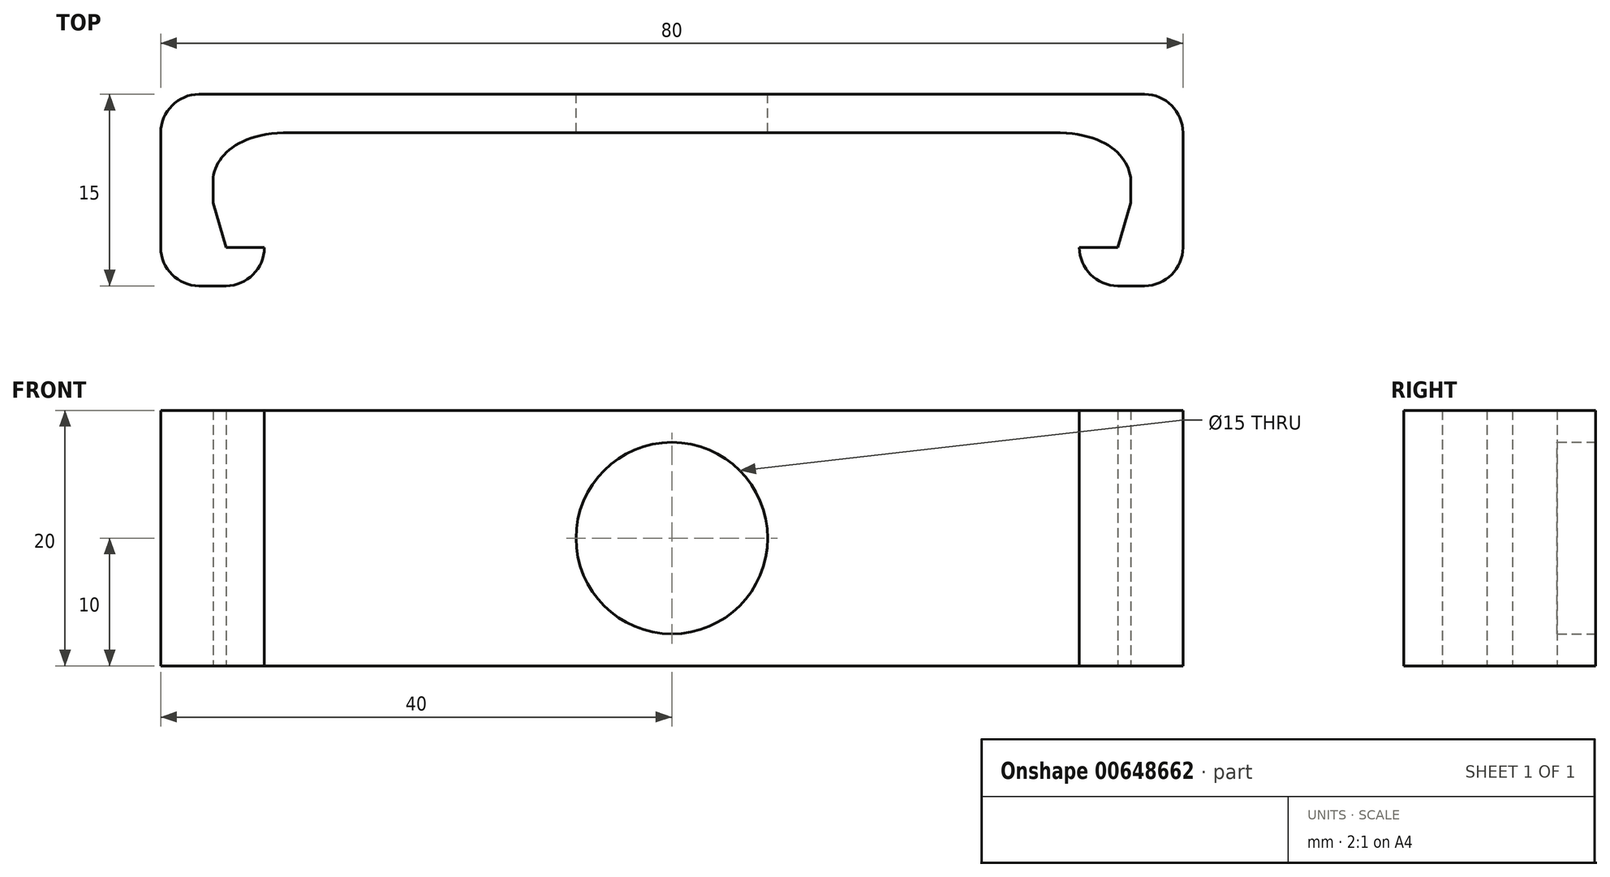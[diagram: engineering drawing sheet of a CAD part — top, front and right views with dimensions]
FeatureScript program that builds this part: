
annotation { "Feature Type Name" : "Feature", "Feature Type Description" : "" }
export const myFeature = defineFeature(function(context is Context, id is Id, definition is map)
    precondition{}
    {
        {
            var Q0;
            Q0=qCreatedBy(makeId("Top.planeOp"),FACE);
            var sketch = newSketch(context, id + "F0", { "sketchPlane" : qUnion([Q0])});
            skLineSegment(sketch, "E0.bottom", {"start": v(37, 7.5) * mm, "end": v(-37, 7.5) * mm});
            skLineSegment(sketch, "E0.top", {"start": v(37, -7.5) * mm, "end": v(34.9, -7.5) * mm});
            skLineSegment(sketch, "E0.left", {"start": v(40, 4.5) * mm, "end": v(40, -4.5) * mm});
            skLineSegment(sketch, "E0.right", {"start": v(-40, 4.5) * mm, "end": v(-40, -4.5) * mm});
            skPoint(sketch, "E0.middle", {"position": v(0, 0) * mm});
            skLineSegment(sketch, "E1.bottom", {"start": v(29.9, 4.5) * mm, "end": v(-29.9, 4.5) * mm});
            skLineSegment(sketch, "E1.top", {"start": v(34.9, -4.5) * mm, "end": v(31.9, -4.5) * mm});
            skLineSegment(sketch, "E1.left", {"start": v(35.9, 1) * mm, "end": v(35.9, -1) * mm});
            skLineSegment(sketch, "E1.right", {"start": v(-35.9, 1) * mm, "end": v(-35.9, -1) * mm});
            skLineSegment(sketch, "E2", {"start": v(-31.9, -4.5) * mm, "end": v(-31.9, -4.5) * mm});
            skLineSegment(sketch, "E3.MirrorCS", {"start": v(31.9, -4.5) * mm, "end": v(31.9, -4.5) * mm});
            skLineSegment(sketch, "E4.trimOffspring", {"start": v(-34.9, -7.5) * mm, "end": v(-37, -7.5) * mm});
            skLineSegment(sketch, "E5.trimOffspring", {"start": v(-31.9, -4.5) * mm, "end": v(-34.9, -4.5) * mm});
            skPoint(sketch, "E6.visualSharp", {"position": v(-40, 7.5) * mm});
            skArc(sketch, "E6.filletArc", {"start": v(-37, 7.5) * mm, "mid": v(-39.12, 6.62) * mm, "end": v(-40, 4.5) * mm});
            skPoint(sketch, "E7.visualSharp", {"position": v(40, 7.5) * mm});
            skArc(sketch, "E7.filletArc", {"start": v(40, 4.5) * mm, "mid": v(39.12, 6.62) * mm, "end": v(37, 7.5) * mm});
            skPoint(sketch, "E8.visualSharp", {"position": v(40, -7.5) * mm});
            skArc(sketch, "E8.filletArc", {"start": v(37, -7.5) * mm, "mid": v(39.12, -6.62) * mm, "end": v(40, -4.5) * mm});
            skPoint(sketch, "E9.visualSharp", {"position": v(-31.9, -7.5) * mm});
            skArc(sketch, "E9.filletArc", {"start": v(-34.9, -7.5) * mm, "mid": v(-32.78, -6.62) * mm, "end": v(-31.9, -4.5) * mm});
            skPoint(sketch, "E10.visualSharp", {"position": v(31.9, -7.5) * mm});
            skArc(sketch, "E10.filletArc", {"start": v(31.9, -4.5) * mm, "mid": v(32.78, -6.62) * mm, "end": v(34.9, -7.5) * mm});
            skPoint(sketch, "E11.visualSharp", {"position": v(-35.9, -4.5) * mm});
            skPoint(sketch, "E12.visualSharp", {"position": v(35.9, -4.5) * mm});
            skFitSpline(sketch, "E13", {"points": [v(-29.9, 4.5) * mm, v(-35.9, 1) * mm], "startDerivative": vector(-11.86, 0) * mm, "endDerivative": vector(-0.76, -5.27) * mm});
            skFitSpline(sketch, "E14.MirrorCS", {"points": [v(29.9, 4.5) * mm, v(35.9, 1) * mm], "startDerivative": vector(11.86, 0) * mm, "endDerivative": vector(0.76, -5.27) * mm});
            skPoint(sketch, "E15.orphan", {"position": v(-35.9, 4.5) * mm});
            skPoint(sketch, "E16.orphan", {"position": v(35.9, 4.5) * mm});
            skLineSegment(sketch, "E17", {"start": v(-35.9, -1) * mm, "end": v(-34.9, -4.5) * mm});
            skLineSegment(sketch, "E18.MirrorCS", {"start": v(35.9, -1) * mm, "end": v(34.9, -4.5) * mm});
            skPoint(sketch, "E19.visualSharp", {"position": v(-40, -7.5) * mm});
            skArc(sketch, "E19.filletArc", {"start": v(-40, -4.5) * mm, "mid": v(-39.12, -6.62) * mm, "end": v(-37, -7.5) * mm});
            skSolve(sketch);
        }
        {
            var Q0;
            Q0 = qSketchRegion(id + "F0", true);
            extrude(context, id + "F1", {"entities" : qUnion([Q0]), "depth" : 20 * mm, "offsetDistance" : 25 * mm});
        }
        {
            var Q0;
            Q0=makeQuery(id+"F1.opExtrude","SWEPT_FACE",FACE,{"disambiguationData":[OSD([sQuery(id+"F0.wireOp",EDGE,"E0.bottom")])]});
            var sketch = newSketch(context, id + "F2", { "sketchPlane" : qUnion([Q0])});
            skCircle(sketch, "E20", {"center": v(0, 10) * mm, "radius": 7.5 * mm});
            skSolve(sketch);
        }
        {
            var Q0;
            Q0 = qSketchRegion(id + "F2", true);
            extrude(context, id + "F3", {"entities" : qUnion([Q0]), "operationType" : NewBodyOperationType.REMOVE, "oppositeDirection" : true, "depth" : 25 * mm, "offsetDistance" : 25 * mm});
        }
    });
